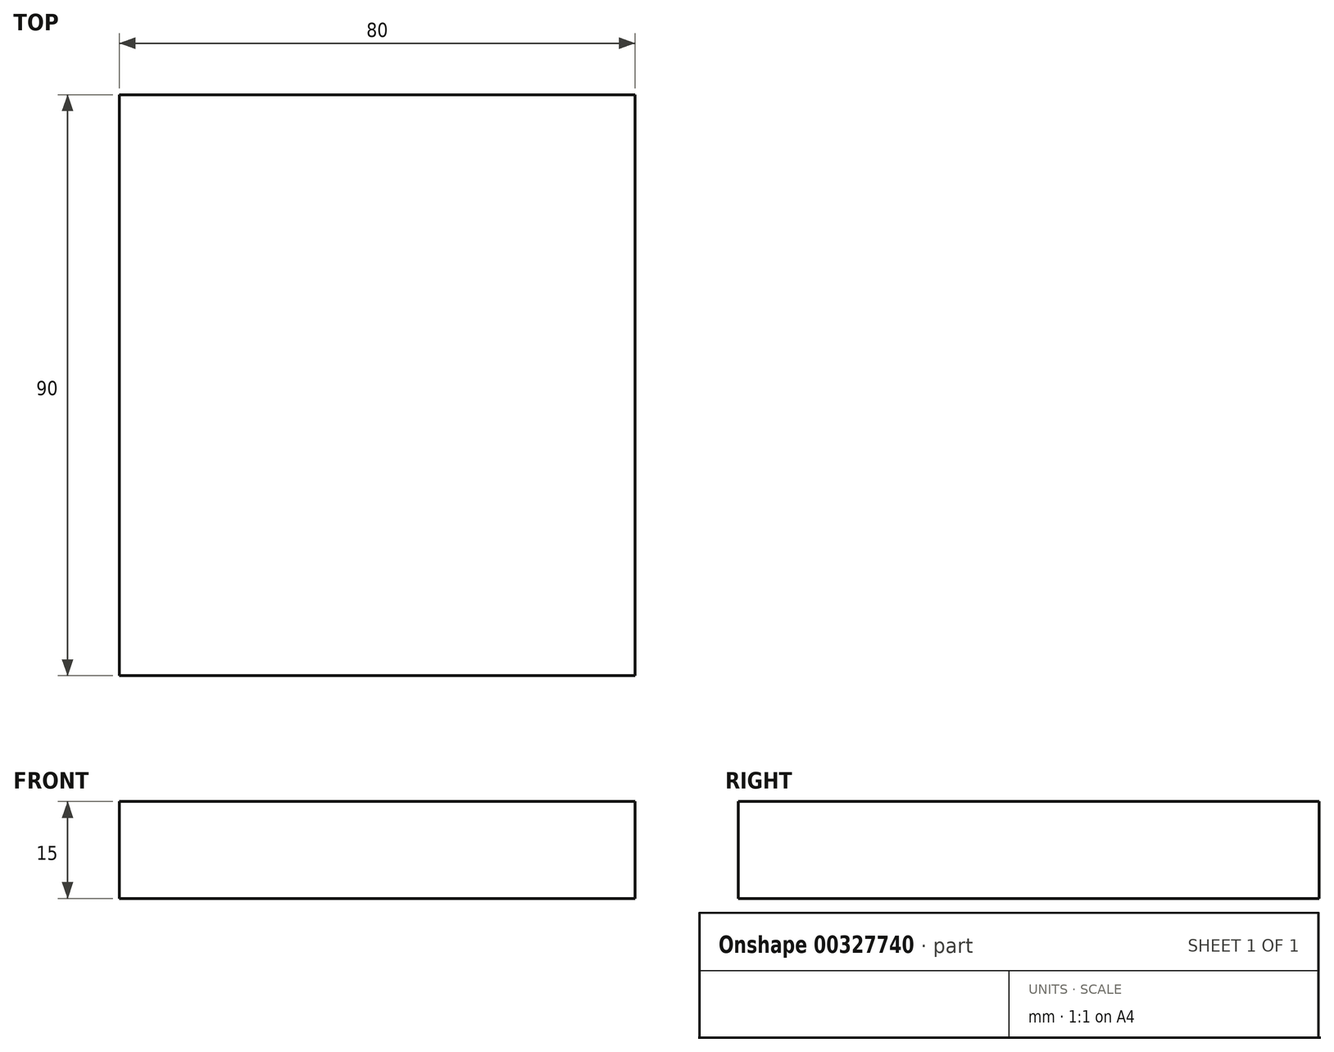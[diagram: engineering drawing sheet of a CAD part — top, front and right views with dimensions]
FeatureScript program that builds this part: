
annotation { "Feature Type Name" : "Feature", "Feature Type Description" : "" }
export const myFeature = defineFeature(function(context is Context, id is Id, definition is map)
    precondition{}
    {
        {
            var Q0;
            Q0=qCreatedBy(makeId("Top.planeOp"),FACE);
            var sketch = newSketch(context, id + "F0", { "sketchPlane" : qUnion([Q0])});
            skLineSegment(sketch, "E0.bottom", {"start": v(40, -45) * mm, "end": v(-40, -45) * mm});
            skLineSegment(sketch, "E0.top", {"start": v(40, 45) * mm, "end": v(-40, 45) * mm});
            skLineSegment(sketch, "E0.left", {"start": v(40, -45) * mm, "end": v(40, 45) * mm});
            skLineSegment(sketch, "E0.right", {"start": v(-40, -45) * mm, "end": v(-40, 45) * mm});
            skPoint(sketch, "E0.middle", {"position": v(0, 0) * mm});
            skSolve(sketch);
        }
        {
            var Q0;
            Q0=makeQuery(id+"F0.imprint","IMPRINT",FACE,{"disambiguationData":[TD([[makeQuery(id+"F0.imprint","IMPRINT",EDGE,{"derivedFrom":sQuery(id+"F0.wireOp",EDGE,"E0.bottom")}),-1.0]])]});
            extrude(context, id + "F1", {"entities" : qUnion([Q0]), "depth" : 15 * mm});
        }
    });
